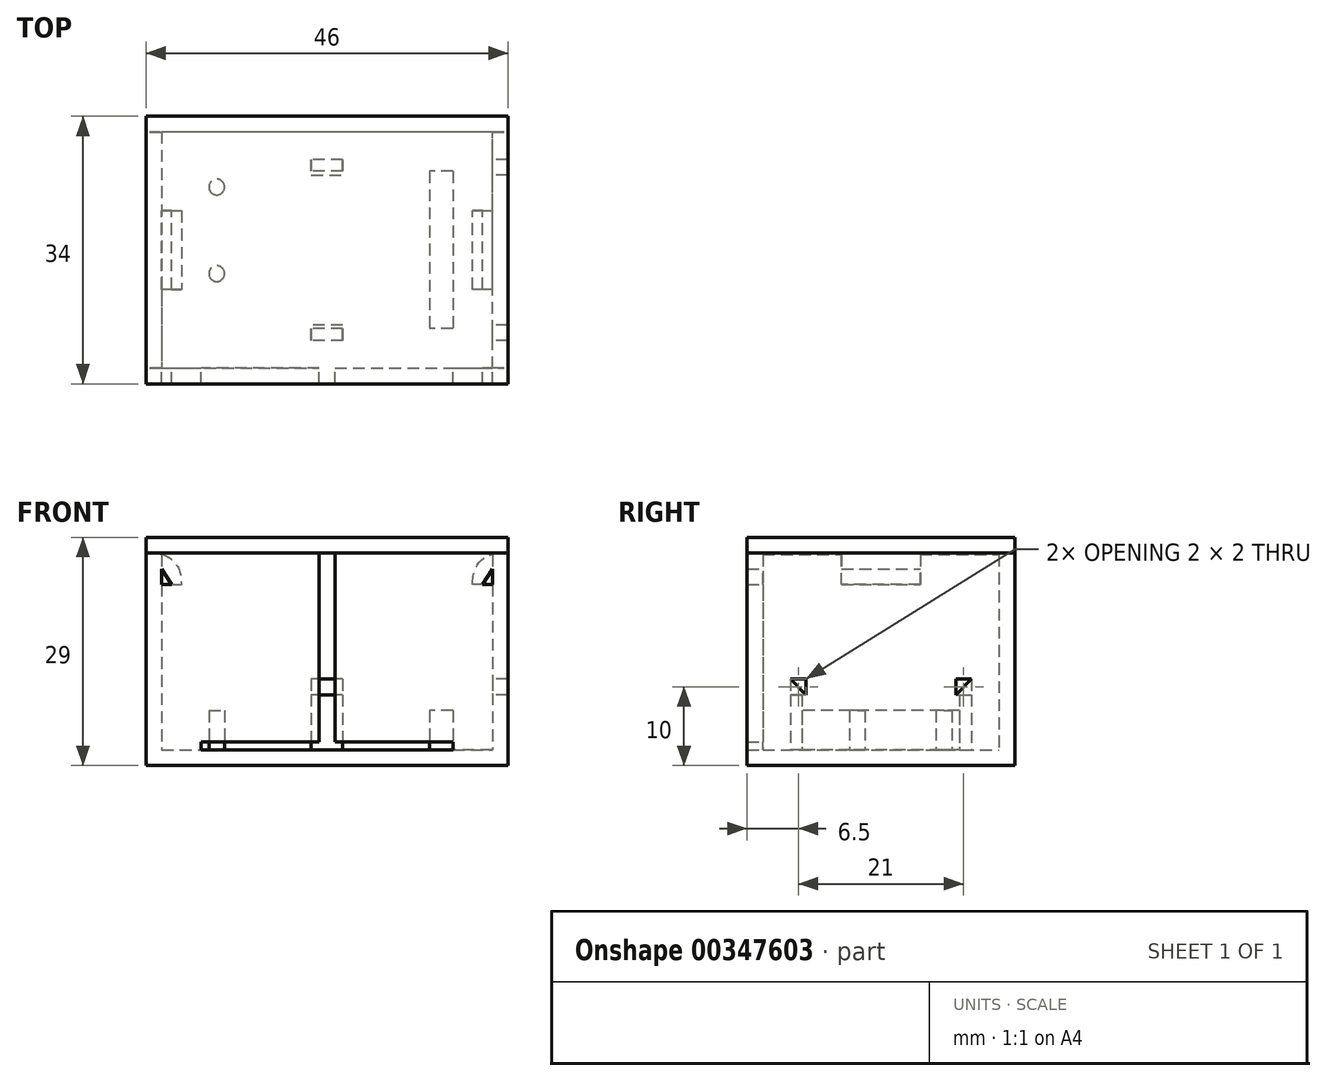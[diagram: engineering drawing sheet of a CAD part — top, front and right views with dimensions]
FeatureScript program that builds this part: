
annotation { "Feature Type Name" : "Feature", "Feature Type Description" : "" }
export const myFeature = defineFeature(function(context is Context, id is Id, definition is map)
    precondition{}
    {
        {
            var Q0;
            Q0=qCreatedBy(makeId("Top.planeOp"),FACE);
            var sketch = newSketch(context, id + "F0", { "sketchPlane" : qUnion([Q0])});
            skLineSegment(sketch, "E0.bottom", {"start": v(16, 10) * mm, "end": v(-16, 10) * mm});
            skLineSegment(sketch, "E0.top", {"start": v(16, -10) * mm, "end": v(-16, -10) * mm});
            skLineSegment(sketch, "E0.left", {"start": v(16, 10) * mm, "end": v(16, -10) * mm});
            skLineSegment(sketch, "E0.right", {"start": v(-16, 10) * mm, "end": v(-16, -10) * mm});
            skPoint(sketch, "E0.middle", {"position": v(0, 0) * mm});
            skSolve(sketch);
        }
        {
            var Q0;
            Q0=qCreatedBy(makeId("Top.planeOp"),FACE);
            var sketch = newSketch(context, id + "F1", { "sketchPlane" : qUnion([Q0])});
            skLineSegment(sketch, "E1.0", {"start": v(-21, -15) * mm, "end": v(21, -15) * mm});
            skLineSegment(sketch, "E1.1", {"start": v(-21, 15) * mm, "end": v(-21, -15) * mm});
            skLineSegment(sketch, "E1.2", {"start": v(21, 15) * mm, "end": v(-21, 15) * mm});
            skLineSegment(sketch, "E1.3", {"start": v(21, -15) * mm, "end": v(21, 15) * mm});
            skLineSegment(sketch, "E2.0", {"start": v(-23, 17) * mm, "end": v(-23, -17) * mm});
            skLineSegment(sketch, "E2.1", {"start": v(23, 17) * mm, "end": v(-23, 17) * mm});
            skLineSegment(sketch, "E2.2", {"start": v(23, -17) * mm, "end": v(23, 17) * mm});
            skLineSegment(sketch, "E2.3", {"start": v(-23, -17) * mm, "end": v(23, -17) * mm});
            skSolve(sketch);
        }
        {
            var Q0;
            Q0=makeQuery(id+"F1.imprint","IMPRINT",FACE,{"disambiguationData":[TD([[makeQuery(id+"F1.imprint","IMPRINT",EDGE,{"derivedFrom":sQuery(id+"F1.wireOp",EDGE,"E1.0")}),-1.0]])]});
            extrude(context, id + "F2", {"entities" : qUnion([Q0]), "depth" : 25 * mm});
        }
        {
            var Q0;
            Q0=makeQuery(id+"F2.opExtrude","CAP_FACE",FACE,{"disambiguationData":[OSD([sQuery(id+"F1.wireOp",EDGE,"E1.0"),sQuery(id+"F1.wireOp",EDGE,"E1.1"),sQuery(id+"F1.wireOp",EDGE,"E1.2"),sQuery(id+"F1.wireOp",EDGE,"E1.3"),sQuery(id+"F1.wireOp",EDGE,"E2.0"),sQuery(id+"F1.wireOp",EDGE,"E2.1"),sQuery(id+"F1.wireOp",EDGE,"E2.2"),sQuery(id+"F1.wireOp",EDGE,"E2.3")])],"isStart":true});
            var sketch = newSketch(context, id + "F3", { "sketchPlane" : qUnion([Q0])});
            skPoint(sketch, "E3.0", {"position": v(23, 17) * mm});
            skLineSegment(sketch, "E3.1", {"start": v(23, 17) * mm, "end": v(23, -17) * mm});
            skLineSegment(sketch, "E3.2", {"start": v(23, -17) * mm, "end": v(-23, -17) * mm});
            skLineSegment(sketch, "E3.3", {"start": v(-23, -17) * mm, "end": v(-23, 17) * mm});
            skLineSegment(sketch, "E3.4", {"start": v(-23, 17) * mm, "end": v(23, 17) * mm});
            skSolve(sketch);
        }
        {
            var Q0;
            Q0 = qSketchRegion(id + "F3", true);
            extrude(context, id + "F4", {"entities" : qUnion([Q0]), "operationType" : NewBodyOperationType.ADD, "depth" : 2 * mm});
        }
        {
            var Q0;
            Q0=makeQuery(id+"F4.opExtrude","CAP_FACE",FACE,{"disambiguationData":[OSD([sQuery(id+"F3.wireOp",EDGE,"E3.1"),sQuery(id+"F3.wireOp",EDGE,"E3.2"),sQuery(id+"F3.wireOp",EDGE,"E3.3"),sQuery(id+"F3.wireOp",EDGE,"E3.4")])],"isStart":true});
            var sketch = newSketch(context, id + "F5", { "sketchPlane" : qUnion([Q0])});
            skPoint(sketch, "E4.0", {"position": v(-16, 10) * mm});
            skLineSegment(sketch, "E5", {"start": v(-16, 10) * mm, "end": v(-14, 10) * mm, "construction": true});
            skLineSegment(sketch, "E6", {"start": v(-14, 10) * mm, "end": v(-14, 8) * mm, "construction": true});
            skCircle(sketch, "E7", {"center": v(-14, 8) * mm, "radius": 1 * mm});
            skLineSegment(sketch, "E8.0", {"start": v(16, -10) * mm, "end": v(-16, -10) * mm});
            skPoint(sketch, "E8.1", {"position": v(-16, -10) * mm});
            skLineSegment(sketch, "E9", {"start": v(-14, 8) * mm, "end": v(-14, -10) * mm, "construction": true});
            skLineSegment(sketch, "E10", {"start": v(-14, -10) * mm, "end": v(-14, -3) * mm, "construction": true});
            skCircle(sketch, "E11", {"center": v(-14, -3) * mm, "radius": 1 * mm});
            skPoint(sketch, "E12.0", {"position": v(16, 10) * mm});
            skLineSegment(sketch, "E13.bottom", {"start": v(16, 10) * mm, "end": v(13, 10) * mm});
            skLineSegment(sketch, "E13.top", {"start": v(16, -10) * mm, "end": v(13, -10) * mm});
            skLineSegment(sketch, "E13.left", {"start": v(16, 10) * mm, "end": v(16, -10) * mm});
            skLineSegment(sketch, "E13.right", {"start": v(13, 10) * mm, "end": v(13, -10) * mm});
            skSolve(sketch);
        }
        {
            var Q0;
            Q0 = qSketchRegion(id + "F5", true);
            extrude(context, id + "F6", {"entities" : qUnion([Q0]), "operationType" : NewBodyOperationType.ADD, "depth" : 5 * mm});
        }
        {
            var Q0;
            Q0=makeQuery(id+"F4.opExtrude","CAP_FACE",FACE,{"disambiguationData":[OSD([sQuery(id+"F3.wireOp",EDGE,"E3.1"),sQuery(id+"F3.wireOp",EDGE,"E3.2"),sQuery(id+"F3.wireOp",EDGE,"E3.3"),sQuery(id+"F3.wireOp",EDGE,"E3.4")])],"isStart":true});
            var sketch = newSketch(context, id + "F7", { "sketchPlane" : qUnion([Q0])});
            skPoint(sketch, "E14.0", {"position": v(-16, 10) * mm});
            skPoint(sketch, "E14.1", {"position": v(16, 10) * mm});
            skLineSegment(sketch, "E15", {"start": v(-16, 10) * mm, "end": v(16, 10) * mm, "construction": true});
            skLineSegment(sketch, "E16", {"start": v(0, 10) * mm, "end": v(2, 10) * mm, "construction": true});
            skLineSegment(sketch, "E17.bottom", {"start": v(2, 10) * mm, "end": v(-2, 10) * mm});
            skLineSegment(sketch, "E17.top", {"start": v(2, 11.5) * mm, "end": v(-2, 11.5) * mm});
            skLineSegment(sketch, "E17.left", {"start": v(2, 10) * mm, "end": v(2, 11.5) * mm});
            skLineSegment(sketch, "E17.right", {"start": v(-2, 10) * mm, "end": v(-2, 11.5) * mm});
            skLineSegment(sketch, "E18.0", {"start": v(16, -10) * mm, "end": v(-16, -10) * mm, "construction": true});
            skLineSegment(sketch, "E19", {"start": v(0, 10) * mm, "end": v(0, -10) * mm, "construction": true});
            skLineSegment(sketch, "E20", {"start": v(0, -10) * mm, "end": v(2, -10) * mm, "construction": true});
            skLineSegment(sketch, "E21.bottom", {"start": v(2, -10) * mm, "end": v(-2, -10) * mm});
            skLineSegment(sketch, "E21.top", {"start": v(2, -11.5) * mm, "end": v(-2, -11.5) * mm});
            skLineSegment(sketch, "E21.left", {"start": v(2, -10) * mm, "end": v(2, -11.5) * mm});
            skLineSegment(sketch, "E21.right", {"start": v(-2, -10) * mm, "end": v(-2, -11.5) * mm});
            skSolve(sketch);
        }
        {
            var Q0;
            Q0 = qSketchRegion(id + "F7", true);
            extrude(context, id + "F8", {"entities" : qUnion([Q0]), "operationType" : NewBodyOperationType.ADD, "depth" : 7 * mm});
        }
        {
            var Q0;
            Q0=makeQuery(id+"F8.opExtrude","CAP_FACE",FACE,{"disambiguationData":[OSD([sQuery(id+"F7.wireOp",EDGE,"E17.bottom"),sQuery(id+"F7.wireOp",EDGE,"E17.top"),sQuery(id+"F7.wireOp",EDGE,"E17.left"),sQuery(id+"F7.wireOp",EDGE,"E17.right")])],"isStart":false});
            var sketch = newSketch(context, id + "F9", { "sketchPlane" : qUnion([Q0])});
            skLineSegment(sketch, "E22.bottom", {"start": v(-2, 11.5) * mm, "end": v(2, 11.5) * mm});
            skLineSegment(sketch, "E22.top", {"start": v(-2, 9.5) * mm, "end": v(2, 9.5) * mm});
            skLineSegment(sketch, "E22.left", {"start": v(-2, 11.5) * mm, "end": v(-2, 9.5) * mm});
            skLineSegment(sketch, "E22.right", {"start": v(2, 11.5) * mm, "end": v(2, 9.5) * mm});
            skPoint(sketch, "E23.0", {"position": v(2, -11.5) * mm});
            skLineSegment(sketch, "E24.bottom", {"start": v(2, -11.5) * mm, "end": v(-2, -11.5) * mm});
            skLineSegment(sketch, "E24.top", {"start": v(2, -9.5) * mm, "end": v(-2, -9.5) * mm});
            skLineSegment(sketch, "E24.left", {"start": v(2, -11.5) * mm, "end": v(2, -9.5) * mm});
            skLineSegment(sketch, "E24.right", {"start": v(-2, -11.5) * mm, "end": v(-2, -9.5) * mm});
            skSolve(sketch);
        }
        {
            var Q0;
            Q0 = qSketchRegion(id + "F9", true);
            extrude(context, id + "F10", {"entities" : qUnion([Q0]), "depth" : 2 * mm});
        }
        {
            var Q0;
            Q0=makeQuery(id+"F10.opExtrude","SWEPT_FACE",FACE,{"disambiguationData":[OSD([sQuery(id+"F9.wireOp",EDGE,"E22.left")])]});
            var sketch = newSketch(context, id + "F11", { "sketchPlane" : qUnion([Q0])});
            skLineSegment(sketch, "E25.1.0", {"start": v(9.5, 7) * mm, "end": v(11.5, 7) * mm});
            skLineSegment(sketch, "E25.1.1", {"start": v(11.5, 7) * mm, "end": v(11.5, 9) * mm});
            skLineSegment(sketch, "E25.1.2", {"start": v(11.5, 9) * mm, "end": v(9.5, 9) * mm});
            skLineSegment(sketch, "E25.1.3", {"start": v(9.5, 9) * mm, "end": v(9.5, 7) * mm});
            skLineSegment(sketch, "E26", {"start": v(-11.5, 9) * mm, "end": v(-9.5, 7) * mm});
            skLineSegment(sketch, "E27", {"start": v(11.5, 9) * mm, "end": v(9.5, 7) * mm});
            skSolve(sketch);
        }
        {
            var Q0;
            Q0=makeQuery(id+"F11.imprint","IMPRINT",FACE,{"disambiguationData":[TD([[makeQuery(id+"F11.imprint","IMPRINT",EDGE,{"derivedFrom":sQuery(id+"F11.wireOp",EDGE,"E26")}),1.0]])]});
            var Q1;
            Q1=makeQuery(id+"F11.imprint","IMPRINT",FACE,{"disambiguationData":[TD([[makeQuery(id+"F11.imprint","IMPRINT",EDGE,{"derivedFrom":sQuery(id+"F11.wireOp",EDGE,"E25.1.2")}),1.0]])]});
            extrude(context, id + "F12", {"entities" : qUnion([Q0, Q1]), "operationType" : NewBodyOperationType.REMOVE, "oppositeDirection" : true, "depth" : 25 * mm});
        }
        {
            var Q0;
            Q0=makeQuery(id+"F2.opExtrude","SWEPT_FACE",FACE,{"disambiguationData":[OSD([sQuery(id+"F1.wireOp",EDGE,"E1.0")])]});
            var sketch = newSketch(context, id + "F13", { "sketchPlane" : qUnion([Q0])});
            skLineSegment(sketch, "E28", {"start": v(0, 25) * mm, "end": v(-1, 25) * mm});
            skLineSegment(sketch, "E29.bottom", {"start": v(-1, 25) * mm, "end": v(1, 25) * mm});
            skLineSegment(sketch, "E29.top", {"start": v(-1, 0) * mm, "end": v(1, 0) * mm});
            skLineSegment(sketch, "E29.left", {"start": v(-1, 25) * mm, "end": v(-1, 0) * mm});
            skLineSegment(sketch, "E29.right", {"start": v(1, 25) * mm, "end": v(1, 0) * mm});
            skLineSegment(sketch, "E30.bottom", {"start": v(-1, 0) * mm, "end": v(-16, 0) * mm});
            skLineSegment(sketch, "E30.top", {"start": v(-1, 1) * mm, "end": v(-16, 1) * mm});
            skLineSegment(sketch, "E30.left", {"start": v(-1, 0) * mm, "end": v(-1, 1) * mm});
            skLineSegment(sketch, "E30.right", {"start": v(-16, 0) * mm, "end": v(-16, 1) * mm});
            skLineSegment(sketch, "E31.bottom", {"start": v(1, 0) * mm, "end": v(16, 0) * mm});
            skLineSegment(sketch, "E31.top", {"start": v(1, 1) * mm, "end": v(16, 1) * mm});
            skLineSegment(sketch, "E31.left", {"start": v(1, 0) * mm, "end": v(1, 1) * mm});
            skLineSegment(sketch, "E31.right", {"start": v(16, 0) * mm, "end": v(16, 1) * mm});
            skSolve(sketch);
        }
        {
            var Q0;
            Q0 = qSketchRegion(id + "F13", true);
            extrude(context, id + "F14", {"entities" : qUnion([Q0]), "operationType" : NewBodyOperationType.REMOVE, "oppositeDirection" : true, "depth" : 25 * mm});
        }
        {
            var Q0;
            Q0=makeQuery(id+"F2.opExtrude","SWEPT_FACE",FACE,{"disambiguationData":[OSD([sQuery(id+"F1.wireOp",EDGE,"E1.1")])]});
            var sketch = newSketch(context, id + "F15", { "sketchPlane" : qUnion([Q0])});
            skLineSegment(sketch, "E32", {"start": v(0, 25) * mm, "end": v(5, 25) * mm});
            skLineSegment(sketch, "E33.bottom", {"start": v(5, 25) * mm, "end": v(-5, 25) * mm});
            skLineSegment(sketch, "E33.top", {"start": v(5, 23) * mm, "end": v(-5, 23) * mm});
            skLineSegment(sketch, "E33.left", {"start": v(5, 25) * mm, "end": v(5, 23) * mm});
            skLineSegment(sketch, "E33.right", {"start": v(-5, 25) * mm, "end": v(-5, 23) * mm});
            skSolve(sketch);
        }
        {
            var Q0;
            Q0 = qSketchRegion(id + "F15", true);
            extrude(context, id + "F16", {"entities" : qUnion([Q0]), "operationType" : NewBodyOperationType.ADD, "depth" : 1 * mm});
        }
        {
            var Q0;
            Q0=makeQuery(id+"F2.opExtrude","SWEPT_FACE",FACE,{"disambiguationData":[OSD([sQuery(id+"F1.wireOp",EDGE,"E1.3")])]});
            var sketch = newSketch(context, id + "F17", { "sketchPlane" : qUnion([Q0])});
            skLineSegment(sketch, "E34", {"start": v(0, 25) * mm, "end": v(-5, 25) * mm, "construction": true});
            skLineSegment(sketch, "E35.bottom", {"start": v(-5, 25) * mm, "end": v(5, 25) * mm});
            skLineSegment(sketch, "E35.top", {"start": v(-5, 23) * mm, "end": v(5, 23) * mm});
            skLineSegment(sketch, "E35.left", {"start": v(-5, 25) * mm, "end": v(-5, 23) * mm});
            skLineSegment(sketch, "E35.right", {"start": v(5, 25) * mm, "end": v(5, 23) * mm});
            skSolve(sketch);
        }
        {
            var Q0;
            Q0 = qSketchRegion(id + "F17", true);
            extrude(context, id + "F18", {"entities" : qUnion([Q0]), "operationType" : NewBodyOperationType.ADD, "depth" : 1 * mm});
        }
        {
            var Q0;
            Q0=makeQuery(id+"F18.boolean.opBoolean","MERGE",FACE,{"derivedFrom":[makeQuery(id+"F16.boolean.opBoolean","MERGE",FACE,{"derivedFrom":[makeQuery(id+"F2.opExtrude","CAP_FACE",FACE,{"disambiguationData":[OSD([sQuery(id+"F1.wireOp",EDGE,"E1.0"),sQuery(id+"F1.wireOp",EDGE,"E1.1"),sQuery(id+"F1.wireOp",EDGE,"E1.2"),sQuery(id+"F1.wireOp",EDGE,"E1.3"),sQuery(id+"F1.wireOp",EDGE,"E2.0"),sQuery(id+"F1.wireOp",EDGE,"E2.1"),sQuery(id+"F1.wireOp",EDGE,"E2.2"),sQuery(id+"F1.wireOp",EDGE,"E2.3")])],"isStart":false}),makeQuery(id+"F16.opExtrude","SWEPT_FACE",FACE,{"disambiguationData":[OSD([sQuery(id+"F15.wireOp",EDGE,"E33.bottom")])]})]}),makeQuery(id+"F18.opExtrude","SWEPT_FACE",FACE,{"disambiguationData":[OSD([sQuery(id+"F17.wireOp",EDGE,"E35.bottom")])]})]});
            var sketch = newSketch(context, id + "F19", { "sketchPlane" : qUnion([Q0])});
            skLineSegment(sketch, "E36.bottom", {"start": v(-23, 17) * mm, "end": v(23, 17) * mm});
            skLineSegment(sketch, "E36.top", {"start": v(-23, -17) * mm, "end": v(23, -17) * mm});
            skLineSegment(sketch, "E36.left", {"start": v(-23, 17) * mm, "end": v(-23, -17) * mm});
            skLineSegment(sketch, "E36.right", {"start": v(23, 17) * mm, "end": v(23, -17) * mm});
            skSolve(sketch);
        }
        {
            var Q0;
            Q0 = qSketchRegion(id + "F19", true);
            extrude(context, id + "F20", {"entities" : qUnion([Q0]), "depth" : 2 * mm});
        }
        {
            var Q0;
            Q0=makeQuery(id+"F20.opExtrude","CAP_FACE",FACE,{"disambiguationData":[OSD([sQuery(id+"F19.wireOp",EDGE,"E36.bottom"),sQuery(id+"F19.wireOp",EDGE,"E36.top"),sQuery(id+"F19.wireOp",EDGE,"E36.left"),sQuery(id+"F19.wireOp",EDGE,"E36.right")])],"isStart":true});
            var sketch = newSketch(context, id + "F21", { "sketchPlane" : qUnion([Q0])});
            skLineSegment(sketch, "E37.0", {"start": v(20, 5) * mm, "end": v(21, 5) * mm});
            skLineSegment(sketch, "E37.1", {"start": v(20, 5) * mm, "end": v(20, -5) * mm});
            skLineSegment(sketch, "E37.2", {"start": v(20, -5) * mm, "end": v(21, -5) * mm});
            skLineSegment(sketch, "E37.3", {"start": v(-20, -5) * mm, "end": v(-20, 5) * mm});
            skLineSegment(sketch, "E37.4", {"start": v(-20, 5) * mm, "end": v(-21, 5) * mm});
            skLineSegment(sketch, "E37.5", {"start": v(-20, -5) * mm, "end": v(-21, -5) * mm});
            skLineSegment(sketch, "E38.bottom", {"start": v(-20, 5) * mm, "end": v(-18.5, 5) * mm});
            skLineSegment(sketch, "E38.top", {"start": v(-20, -5) * mm, "end": v(-18.5, -5) * mm});
            skLineSegment(sketch, "E38.left", {"start": v(-20, 5) * mm, "end": v(-20, -5) * mm});
            skLineSegment(sketch, "E38.right", {"start": v(-18.5, 5) * mm, "end": v(-18.5, -5) * mm});
            skLineSegment(sketch, "E39.bottom", {"start": v(20, 5) * mm, "end": v(18.5, 5) * mm});
            skLineSegment(sketch, "E39.top", {"start": v(20, -5) * mm, "end": v(18.5, -5) * mm});
            skLineSegment(sketch, "E39.right", {"start": v(18.5, 5) * mm, "end": v(18.5, -5) * mm});
            skSolve(sketch);
        }
        {
            var Q0;
            Q0 = qSketchRegion(id + "F21", true);
            extrude(context, id + "F22", {"entities" : qUnion([Q0]), "depth" : 4 * mm});
        }
        {
            var Q0;
            Q0=makeQuery(id+"F18.opExtrude","SWEPT_FACE",FACE,{"disambiguationData":[OSD([sQuery(id+"F17.wireOp",EDGE,"E35.top")])]});
            var Q1;
            Q1=makeQuery(id+"F16.opExtrude","SWEPT_FACE",FACE,{"disambiguationData":[OSD([sQuery(id+"F15.wireOp",EDGE,"E33.top")])]});
            var Q2;
            Q2=makeQuery(id+"F22.opExtrude","CAP_FACE",FACE,{"disambiguationData":[OSD([sQuery(id+"F21.wireOp",EDGE,"E38.bottom"),sQuery(id+"F21.wireOp",EDGE,"E38.top"),sQuery(id+"F21.wireOp",EDGE,"E38.left"),sQuery(id+"F21.wireOp",EDGE,"E38.right")])],"isStart":false});
            extrude(context, id + "F23", {"entities" : qUnion([Q0, Q1]), "operationType" : NewBodyOperationType.ADD, "endBound" : BoundingType.UP_TO_SURFACE, "endBoundEntityFace" : qUnion([Q2]), "depth" : 25 * mm});
        }
        {
            var Q0;
            Q0=makeQuery(id+"F23.boolean.opBoolean","MERGE",FACE,{"derivedFrom":[makeQuery(id+"F22.opExtrude","SWEPT_FACE",FACE,{"disambiguationData":[OSD([sQuery(id+"F21.wireOp",EDGE,"E39.top")])]}),makeQuery(id+"F23.opExtrude","SWEPT_FACE",FACE,{"disambiguationData":[OSD([sQuery(id+"F17.wireOp",EDGE,"E35.top"),sQuery(id+"F17.wireOp",EDGE,"E35.left")])]})]});
            var sketch = newSketch(context, id + "F24", { "sketchPlane" : qUnion([Q0])});
            skPoint(sketch, "E40.0", {"position": v(-21, 23) * mm});
            skPoint(sketch, "E40.1", {"position": v(-19.75, 21) * mm});
            skLineSegment(sketch, "E41", {"start": v(-19.75, 21) * mm, "end": v(-21, 23) * mm});
            skPoint(sketch, "E42.0", {"position": v(21, 23) * mm});
            skPoint(sketch, "E42.1", {"position": v(19.75, 21) * mm});
            skLineSegment(sketch, "E43", {"start": v(19.75, 21) * mm, "end": v(21, 23) * mm});
            skLineSegment(sketch, "E44.0", {"start": v(21, 21) * mm, "end": v(21, 23) * mm});
            skLineSegment(sketch, "E44.1", {"start": v(21, 21) * mm, "end": v(18.5, 21) * mm});
            skLineSegment(sketch, "E45.0", {"start": v(-21, 21) * mm, "end": v(-18.5, 21) * mm});
            skLineSegment(sketch, "E45.1", {"start": v(-21, 21) * mm, "end": v(-21, 23) * mm});
            skSolve(sketch);
        }
        {
            var Q0;
            {var subQ0=sQuery(id+"F24.wireOp",EDGE,"E41");Q0=makeQuery(id+"F24.imprint","IMPRINT",FACE,{"disambiguationData":[TD([[makeQuery(id+"F24.imprint","IMPRINT",EDGE,{"derivedFrom":subQ0}),1.0]])]});}
            var Q1;
            {var subQ0=sQuery(id+"F24.wireOp",EDGE,"E43");Q1=makeQuery(id+"F24.imprint","IMPRINT",FACE,{"disambiguationData":[TD([[makeQuery(id+"F24.imprint","IMPRINT",EDGE,{"derivedFrom":subQ0}),-1.0]])]});}
            extrude(context, id + "F25", {"entities" : qUnion([Q0, Q1]), "operationType" : NewBodyOperationType.REMOVE, "oppositeDirection" : true, "depth" : 25 * mm});
        }
        {
            var Q0;
            Q0=makeQuery(id+"F22.opExtrude","CAP_EDGE",EDGE,{"disambiguationData":[OSD([sQuery(id+"F21.wireOp",EDGE,"E39.right")])],"isStart":true});
            var Q1;
            Q1=makeQuery(id+"F22.opExtrude","CAP_EDGE",EDGE,{"disambiguationData":[OSD([sQuery(id+"F21.wireOp",EDGE,"E38.right")])],"isStart":true});
            fillet(context, id + "F26", {"entities" : qUnion([Q0, Q1]), "radius" : 4 * mm, "tangentPropagation" : true, "rho" : 0.5, "crossSection" : FilletCrossSection.CONIC, "allowEdgeOverflow" : false});
        }
    });
